# Revit family: Červinka_Hydrantový systém
name_source: partatom
category: Speciální vybavení
units: mm (PartAtom-declared; Revit-internal decimal feet)

## family parameters
Bod výpočtu místnosti = Ne
Kóta kulaté spojky = Použít průměr
Nadpis OmniClass = Inlet/Outlet Valves for Liquid Services
Ořezat dutým tvarem při načtení = Ne
Sdílené = Ne
Typ dílu = Normální
Vždy vertikální = Ano
Založené na pracovní rovině = Ano
Číslo OmniClass = 23.65.55.14.11

## types (2) — shared parameters
Délka hadice_ = 30000 mm  [stored 98.4252 ft]
Komentáře k typům = Jednokřídlý
Kód sestavy = PZ.
Materiál madla = Černá
Materiál skříně = Červená
Popis = Požární hydrant
Provozuschopnost_ = Ano
Splnění norem = Certifikované dle EN 671-1
URL = https://hasicitechnika.com
Výchozí výška = 1219 mm
Výrobce = ČERVINKA - CZECH REPUBLIC s.r.o.
Výška středu zařízení nad podlahou = 1200 mm
Výška_ = 700 mm  [stored 2.29659 ft]
Šířka_ = 700 mm  [stored 2.29659 ft]
zero-valued in all types: Cena, Rok výroby_

## per-type parameters (varying)
| type | Hadice | Hloubka_ | Hmotnost | Jmenovitá světlost hadice_ | Jmenovitý průměr_ | Kód_ |
| D25 | Tvarově stálá hadice DN25/30m - PVC s polyesterovou pryží | 260 mm  [stored 0.853018 ft] | 37.00 kg | 25 mm  [stored 0.082021 ft] | 25 mm | 208 |
| D19 | Tvarově stálá hadice DN19 / 30 m - PVC s polyesterovou pryží | 230 mm  [stored 0.754593 ft] | 30.00 kg | 19 mm  [stored 0.062336 ft] | 19 mm | 209 |

note: column(s) folded — value = type name in every type: Model

note: [stored X ft] marks values corroborated as IEEE doubles in the binary element streams (Revit-internal decimal feet)
